# Revit family: Outdoor_ Upper_Bottle_Filling_Station_Bi-Level_Pedestal_Pet_Station-Elkay-LK4420BF1UDBEVG_BLU_BLK_GRY
name_source: partatom
category: Plumbing Fixtures
units: mm (PartAtom-declared; Revit-internal decimal feet)

## family parameters
Always vertical = Yes
Cut with Voids When Loaded = No
Maintain Annotation Orientation = No
OmniClass Number = 23.45.05.14.14
OmniClass Title = Sinks/Lavatories
Part Type = Normal
Room Calculation Point = No
Round Connector Dimension = Use Diameter
Shared = No
Work Plane-Based = No

## types (4) — shared parameters
Access Panel Length = 10 "
Access Panel Width = 8 "
Activation Method = Mechanical Button
Approx. Shipping Weight (lbs) = 184
Arm Bowl Button = 3.875 "
Assembly Code = D2010
Base Thickness = 0.125 "
Bottle placing Height = 14.563 "
Bottom access panel height = 8 "
Bowl Arm size = 6 "
C/C distance b/w pet bowl and normal Bowl = 12 "
CW Connection = No
Chilling Capacity = Non-refrigerated
Description = Outdoor ezH2O®  Upper Bottle Filling Station Bi-Level Pedestal with Pet Station Non-Filtered Non-Refrigerated
Dimensions (L x W x H) = 26 inch x 31 inch x 64 inch
Height = 64 "
Inlet Connection Size (inch) = 0.375 "
Installation Location = Outdoor
Length = 14 "
Lower_Access panel placing Height = 8 "
Main Bowl button = 4.5 "
Main Material = Finish-Elkay-Stainless Steel
Manufacturer = Elkay (by Zurn Elkay Water Solutions)
Manufacturer Brand = Elkay Manufacturer Company
Mounting Type = Floor Mount/Freestanding
Outlet Connection Size(inch) = 1.5 "
Pet Arm = 6 "
Pet Bowl Button = 14.5 "
Product Documentation Link = https://www.elkayfiles.com
Product Installation Sheet URL = https://www.elkayfiles.com
Product Page URL = https://www.elkay.com
Product Weight (lbs) = 152
Product data URL = https://bimobject.com
Radius of Bowl = 5 "
Repair Parts URL = https://www.elkayfiles.com
URL = https://www.elkay.com
Upper Access panel placing Height = 30 "
Upper access panel height = 30 "
Waste Connection = No
Width = 31 "
angle = 22.00°
zero-valued in all types: CWFU, Default Elevation, HWFU, WFU

## per-type parameters (varying)
| type | Model | Secoundary Material |
| LK4420BF1UDBEVG (Outdoor ezH2O®  Upper Bottle Filling Station Bi-Level Pedestal with Pet Station Non-Filtered Non-Refrigerated) | LK4420BF1UDBEVG | Finish-Elkay-Green |
| LK4420BF1UDBBLU (Outdoor ezH2O®  Upper Bottle Filling Station Bi-Level Pedestal with Pet Station Non-Filtered Non-Refrigerated) | LK4420BF1UDBBLU | Finish- Elkay- Blue |
| LK4420BF1UDBBLK (Outdoor ezH2O®  Upper Bottle Filling Station Bi-Level Pedestal with Pet Station Non-Filtered Non-Refrigerated) | LK4420BF1UDBBLK | Finish-Elkay-Black |
| LK4420BF1UDBGRY (Outdoor ezH2O®  Upper Bottle Filling Station Bi-Level Pedestal with Pet Station Non-Filtered Non-Refrigerated) | LK4420BF1UDBGRY | Finish-Elkay-Gray |

## geometry (parser evidence)
native form markers: Sweep x4
no freeform markers — native parametric forms only
